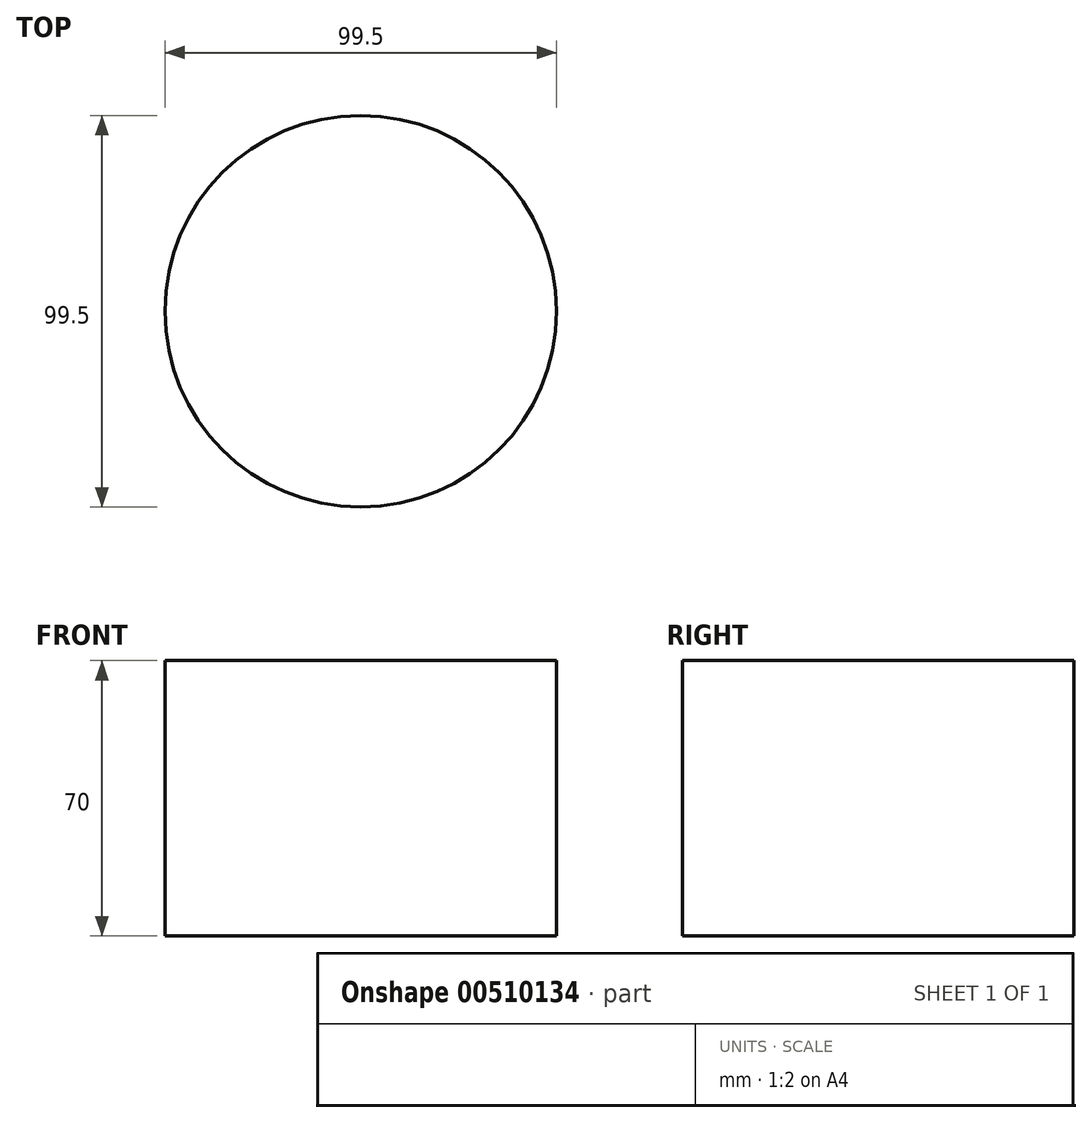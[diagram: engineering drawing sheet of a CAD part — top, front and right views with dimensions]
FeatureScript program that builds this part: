
annotation { "Feature Type Name" : "Feature", "Feature Type Description" : "" }
export const myFeature = defineFeature(function(context is Context, id is Id, definition is map)
    precondition{}
    {
        {
            var Q0;
            Q0=qCreatedBy(makeId("Top.planeOp"),FACE);
            var sketch = newSketch(context, id + "F0", { "sketchPlane" : qUnion([Q0])});
            skCircle(sketch, "E0", {"center": v(0, 0) * mm, "radius": 49.75 * mm});
            skSolve(sketch);
        }
        {
            var Q0;
            Q0=makeQuery(id+"F0.imprint","IMPRINT",FACE,{"disambiguationData":[TD([[makeQuery(id+"F0.imprint","IMPRINT",EDGE,{"derivedFrom":sQuery(id+"F0.wireOp",EDGE,"E0")}),1.0]])]});
            extrude(context, id + "F1", {"entities" : qUnion([Q0]), "depth" : 70 * mm});
        }
    });
